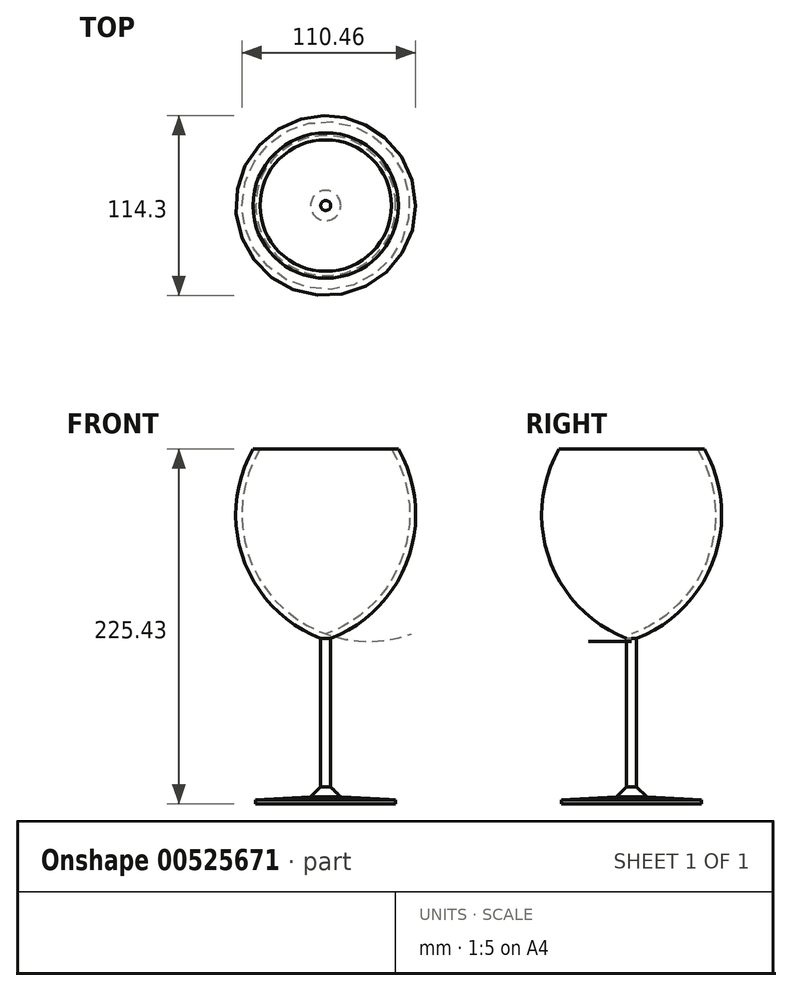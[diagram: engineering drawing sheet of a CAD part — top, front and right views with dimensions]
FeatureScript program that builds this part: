
annotation { "Feature Type Name" : "Feature", "Feature Type Description" : "" }
export const myFeature = defineFeature(function(context is Context, id is Id, definition is map)
    precondition{}
    {
        {
            var Q0;
            Q0=qCreatedBy(makeId("Front.planeOp"),FACE);
            var sketch = newSketch(context, id + "F0", { "sketchPlane" : qUnion([Q0])});
            skLineSegment(sketch, "E0", {"start": v(0, 0) * mm, "end": v(0, -107.95) * mm});
            skLineSegment(sketch, "E1", {"start": v(0, -107.95) * mm, "end": v(44.45, -107.95) * mm});
            skLineSegment(sketch, "E2", {"start": v(44.45, -107.95) * mm, "end": v(44.45, -105.4) * mm});
            skLineSegment(sketch, "E3", {"start": v(44.45, -105.4) * mm, "end": v(9.57, -103.58) * mm});
            skLineSegment(sketch, "E4", {"start": v(9.57, -103.58) * mm, "end": v(3.17, -97.18) * mm});
            skLineSegment(sketch, "E5", {"start": v(3.18, -97.18) * mm, "end": v(3.18, -2.9) * mm});
            skArc(sketch, "E6", {"start": v(3.18, -2.9) * mm, "mid": v(52.23, 47.44) * mm, "end": v(46.18, 117.48) * mm});
            skArc(sketch, "E7", {"start": v(0, 0) * mm, "mid": v(48.66, 48.86) * mm, "end": v(41.74, 117.48) * mm});
            skLineSegment(sketch, "E8", {"start": v(41.74, 117.48) * mm, "end": v(46.18, 117.48) * mm});
            skSolve(sketch);
        }
        {
            var Q0;
            Q0 = qSketchRegion(id + "F0", true);
            var Q1;
            Q1=sQuery(id+"F0.wireOp",EDGE,"E0");
            revolve(context, id + "F1", {"entities" : qUnion([Q0]), "axis" : qUnion([Q1]), "revolveType" : RevolveType.FULL});
        }
    });
